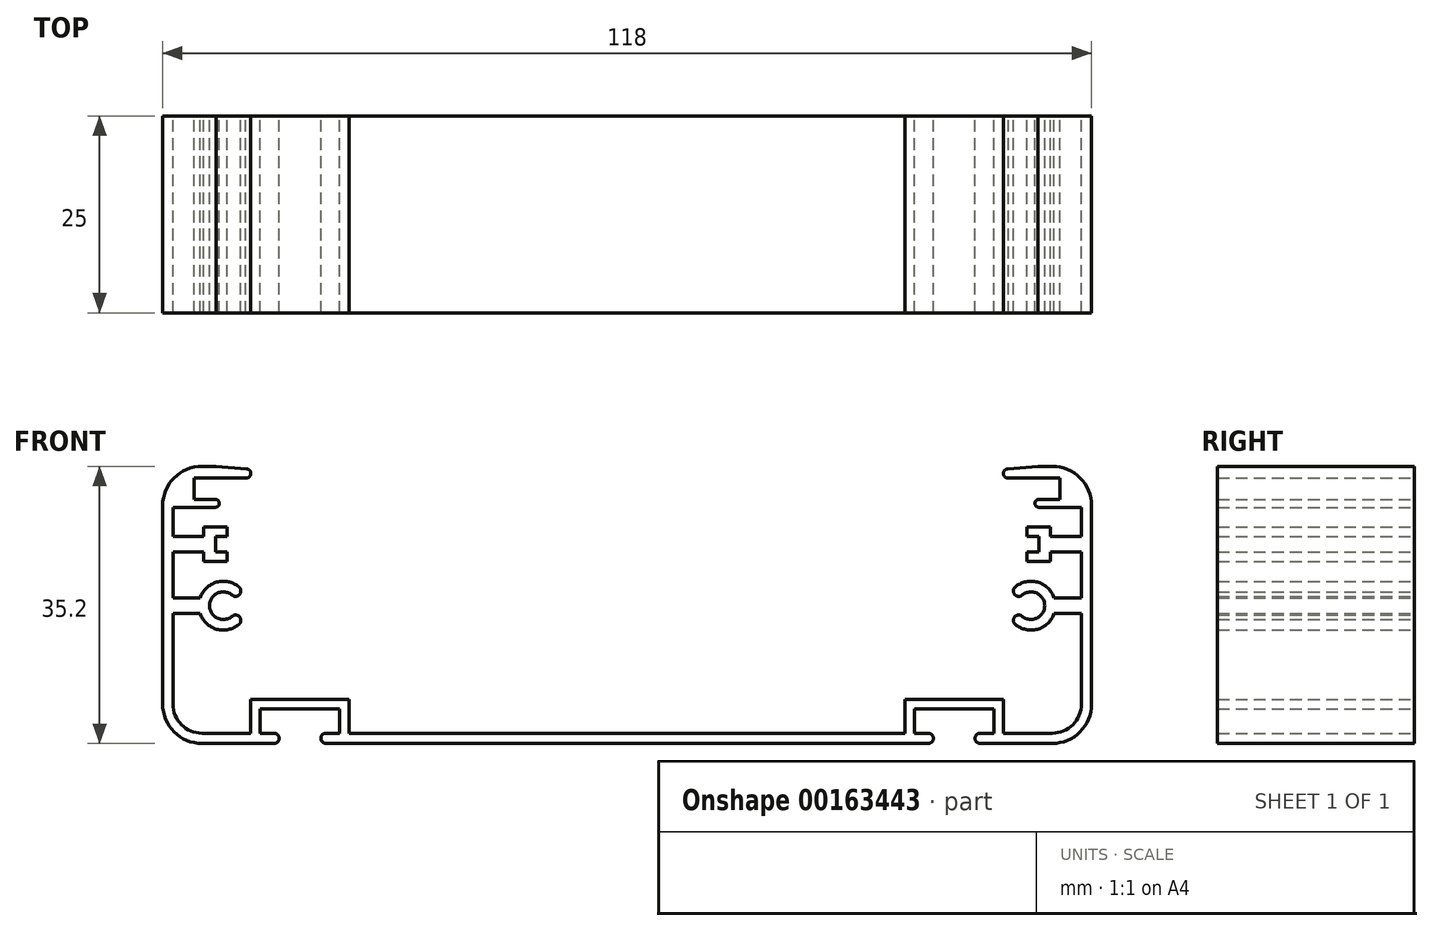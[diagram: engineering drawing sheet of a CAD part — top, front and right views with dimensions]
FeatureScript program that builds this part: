
annotation { "Feature Type Name" : "Feature", "Feature Type Description" : "" }
export const myFeature = defineFeature(function(context is Context, id is Id, definition is map)
    precondition{}
    {
        {
            var Q0;
            Q0=qCreatedBy(makeId("Front.planeOp"),FACE);
            var sketch = newSketch(context, id + "F0", { "sketchPlane" : qUnion([Q0])});
            skLineSegment(sketch, "E0", {"start": v(0, 1.3) * mm, "end": v(0, 0) * mm});
            skLineSegment(sketch, "E1", {"start": v(0, 0) * mm, "end": v(-38.25, 0) * mm});
            skLineSegment(sketch, "E2", {"start": v(-38.25, 1.3) * mm, "end": v(-36.5, 1.3) * mm});
            skLineSegment(sketch, "E3", {"start": v(-36.5, 1.3) * mm, "end": v(-36.5, 4.4) * mm});
            skLineSegment(sketch, "E4", {"start": v(-36.5, 4.4) * mm, "end": v(-46.6, 4.4) * mm});
            skLineSegment(sketch, "E5", {"start": v(-46.6, 4.4) * mm, "end": v(-46.6, 1.3) * mm});
            skLineSegment(sketch, "E6", {"start": v(-46.6, 1.3) * mm, "end": v(-44.85, 1.3) * mm});
            skLineSegment(sketch, "E7", {"start": v(0, 1.3) * mm, "end": v(-35.3, 1.3) * mm});
            skLineSegment(sketch, "E8", {"start": v(-35.3, 1.3) * mm, "end": v(-35.3, 5.6) * mm});
            skLineSegment(sketch, "E9", {"start": v(-35.3, 5.6) * mm, "end": v(-47.8, 5.6) * mm});
            skLineSegment(sketch, "E10", {"start": v(-47.8, 5.6) * mm, "end": v(-47.8, 1.3) * mm});
            skLineSegment(sketch, "E11", {"start": v(-47.8, 1.3) * mm, "end": v(-54, 1.3) * mm});
            skLineSegment(sketch, "E12", {"start": v(-54, 35.2) * mm, "end": v(-52.2, 35.2) * mm});
            skLineSegment(sketch, "E13", {"start": v(-52.2, 35.2) * mm, "end": v(-48.35, 34.9) * mm});
            skLineSegment(sketch, "E14", {"start": v(-48.45, 33.7) * mm, "end": v(-55, 33.7) * mm});
            skLineSegment(sketch, "E15", {"start": v(-55, 33.7) * mm, "end": v(-55, 31) * mm});
            skLineSegment(sketch, "E16", {"start": v(-55, 31) * mm, "end": v(-52.3, 31) * mm});
            skLineSegment(sketch, "E17", {"start": v(-52.3, 30) * mm, "end": v(-57.7, 30) * mm});
            skLineSegment(sketch, "E18", {"start": v(-57.7, 30) * mm, "end": v(-57.7, 26.3) * mm});
            skLineSegment(sketch, "E19", {"start": v(-57.7, 26.3) * mm, "end": v(-53.8, 26.3) * mm});
            skLineSegment(sketch, "E20", {"start": v(-53.8, 26.3) * mm, "end": v(-53.8, 27.5) * mm});
            skLineSegment(sketch, "E21", {"start": v(-53.8, 27.5) * mm, "end": v(-50.8, 27.5) * mm});
            skLineSegment(sketch, "E22", {"start": v(-50.8, 26.3) * mm, "end": v(-52.3, 26.3) * mm});
            skLineSegment(sketch, "E23", {"start": v(-52.3, 26.3) * mm, "end": v(-52.3, 24.3) * mm});
            skLineSegment(sketch, "E24", {"start": v(-52.3, 24.3) * mm, "end": v(-50.8, 24.3) * mm});
            skLineSegment(sketch, "E25", {"start": v(-50.8, 23.1) * mm, "end": v(-53.8, 23.1) * mm});
            skLineSegment(sketch, "E26", {"start": v(-53.8, 23.1) * mm, "end": v(-53.8, 24.3) * mm});
            skLineSegment(sketch, "E27", {"start": v(-53.8, 24.3) * mm, "end": v(-57.7, 24.3) * mm});
            skLineSegment(sketch, "E28", {"start": v(-57.7, 24.3) * mm, "end": v(-57.7, 18.5) * mm});
            skLineSegment(sketch, "E29", {"start": v(-57.7, 18.5) * mm, "end": v(-54.23, 18.5) * mm});
            skLineSegment(sketch, "E30", {"start": v(-54.23, 16.5) * mm, "end": v(-57.7, 16.5) * mm});
            skArc(sketch, "E31", {"start": v(-52.3, 30) * mm, "mid": v(-51.8, 30.5) * mm, "end": v(-52.3, 31) * mm});
            skArc(sketch, "E32", {"start": v(-44.85, 0) * mm, "mid": v(-44.2, 0.65) * mm, "end": v(-44.85, 1.3) * mm});
            skArc(sketch, "E33", {"start": v(-38.25, 1.3) * mm, "mid": v(-38.9, 0.65) * mm, "end": v(-38.25, 0) * mm});
            skLineSegment(sketch, "E34", {"start": v(-57.7, 16.5) * mm, "end": v(-57.7, 5) * mm});
            skPoint(sketch, "E35.visualSharp", {"position": v(-57.7, 1.3) * mm});
            skArc(sketch, "E35.filletArc", {"start": v(-57.7, 5) * mm, "mid": v(-56.62, 2.38) * mm, "end": v(-54, 1.3) * mm});
            skLineSegment(sketch, "E36", {"start": v(-59, 30.2) * mm, "end": v(-59, 5) * mm});
            skLineSegment(sketch, "E37", {"start": v(-54, 0) * mm, "end": v(-44.85, 0) * mm});
            skPoint(sketch, "E38.visualSharp", {"position": v(-59, 0) * mm});
            skArc(sketch, "E38.filletArc", {"start": v(-59, 5) * mm, "mid": v(-57.54, 1.46) * mm, "end": v(-54, 0) * mm});
            skPoint(sketch, "E39.visualSharp", {"position": v(-59, 35.2) * mm});
            skArc(sketch, "E39.filletArc", {"start": v(-54, 35.2) * mm, "mid": v(-57.54, 33.74) * mm, "end": v(-59, 30.2) * mm});
            skArc(sketch, "E40", {"start": v(-48.45, 33.7) * mm, "mid": v(-47.8, 34.25) * mm, "end": v(-48.35, 34.9) * mm});
            skLineSegment(sketch, "E41", {"start": v(-50.8, 27.5) * mm, "end": v(-50.8, 26.3) * mm});
            skLineSegment(sketch, "E42", {"start": v(-50.8, 24.3) * mm, "end": v(-50.8, 23.1) * mm});
            skArc(sketch, "E43", {"start": v(-54.23, 16.5) * mm, "mid": v(-52.13, 14.51) * mm, "end": v(-49.3, 15.13) * mm});
            skArc(sketch, "E44", {"start": v(-50.18, 18.84) * mm, "mid": v(-53.05, 17.5) * mm, "end": v(-50.18, 16.16) * mm});
            skArc(sketch, "E45", {"start": v(-50.18, 18.84) * mm, "mid": v(-49.22, 18.92) * mm, "end": v(-49.3, 19.87) * mm});
            skArc(sketch, "E46", {"start": v(-49.3, 15.13) * mm, "mid": v(-49.22, 16.08) * mm, "end": v(-50.18, 16.16) * mm});
            skLineSegment(sketch, "E47", {"start": v(-49.74, 19.36) * mm, "end": v(-51.3, 17.5) * mm, "construction": true});
            skLineSegment(sketch, "E48", {"start": v(-49.74, 15.64) * mm, "end": v(-51.3, 17.5) * mm, "construction": true});
            skArc(sketch, "E49.trimOffspring", {"start": v(-49.3, 19.87) * mm, "mid": v(-52.13, 20.49) * mm, "end": v(-54.23, 18.5) * mm});
            skLineSegment(sketch, "E50", {"start": v(-51.3, 17.5) * mm, "end": v(-45.16, 17.5) * mm, "construction": true});
            skSolve(sketch);
        }
        {
            var Q0;
            Q0 = qSketchRegion(id + "F0", true);
            extrude(context, id + "F1", {"entities" : qUnion([Q0]), "depth" : 25 * mm});
        }
        {
            var Q0;
            Q0=makeQuery(id+"F1.opExtrude","SWEPT_BODY",BODY,{"disambiguationData":[OSD([sQuery(id+"F0.wireOp",EDGE,"E0"),sQuery(id+"F0.wireOp",EDGE,"E1"),sQuery(id+"F0.wireOp",EDGE,"E2"),sQuery(id+"F0.wireOp",EDGE,"E3"),sQuery(id+"F0.wireOp",EDGE,"E4"),sQuery(id+"F0.wireOp",EDGE,"E5"),sQuery(id+"F0.wireOp",EDGE,"E6"),sQuery(id+"F0.wireOp",EDGE,"E7"),sQuery(id+"F0.wireOp",EDGE,"E8"),sQuery(id+"F0.wireOp",EDGE,"E9"),sQuery(id+"F0.wireOp",EDGE,"E10"),sQuery(id+"F0.wireOp",EDGE,"E11"),sQuery(id+"F0.wireOp",EDGE,"E12"),sQuery(id+"F0.wireOp",EDGE,"E13"),sQuery(id+"F0.wireOp",EDGE,"E14"),sQuery(id+"F0.wireOp",EDGE,"E15"),sQuery(id+"F0.wireOp",EDGE,"E16"),sQuery(id+"F0.wireOp",EDGE,"E17"),sQuery(id+"F0.wireOp",EDGE,"E18"),sQuery(id+"F0.wireOp",EDGE,"E19"),sQuery(id+"F0.wireOp",EDGE,"E20"),sQuery(id+"F0.wireOp",EDGE,"E21"),sQuery(id+"F0.wireOp",EDGE,"E22"),sQuery(id+"F0.wireOp",EDGE,"E23"),sQuery(id+"F0.wireOp",EDGE,"E24"),sQuery(id+"F0.wireOp",EDGE,"E25"),sQuery(id+"F0.wireOp",EDGE,"E26"),sQuery(id+"F0.wireOp",EDGE,"E27"),sQuery(id+"F0.wireOp",EDGE,"E28"),sQuery(id+"F0.wireOp",EDGE,"E29"),sQuery(id+"F0.wireOp",EDGE,"E30"),sQuery(id+"F0.wireOp",EDGE,"E31"),sQuery(id+"F0.wireOp",EDGE,"E32"),sQuery(id+"F0.wireOp",EDGE,"E33"),sQuery(id+"F0.wireOp",EDGE,"E34"),sQuery(id+"F0.wireOp",EDGE,"E35.filletArc"),sQuery(id+"F0.wireOp",EDGE,"E36"),sQuery(id+"F0.wireOp",EDGE,"E37"),sQuery(id+"F0.wireOp",EDGE,"E38.filletArc"),sQuery(id+"F0.wireOp",EDGE,"E39.filletArc"),sQuery(id+"F0.wireOp",EDGE,"E40"),sQuery(id+"F0.wireOp",EDGE,"E41"),sQuery(id+"F0.wireOp",EDGE,"E42"),sQuery(id+"F0.wireOp",EDGE,"E43"),sQuery(id+"F0.wireOp",EDGE,"E44"),sQuery(id+"F0.wireOp",EDGE,"E45"),sQuery(id+"F0.wireOp",EDGE,"E46"),sQuery(id+"F0.wireOp",EDGE,"E49.trimOffspring")])]});
            var Q1;
            Q1=qCreatedBy(makeId("Right.planeOp"),FACE);
            mirror(context, id + "F2", {"operationType" : NewBodyOperationType.ADD, "entities" : qUnion([Q0]), "mirrorPlane" : qUnion([Q1])});
        }
    });
